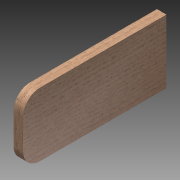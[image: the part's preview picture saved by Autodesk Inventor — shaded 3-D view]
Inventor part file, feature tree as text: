
AUTODESK INVENTOR PART (.ipt)
format: ipt  version: 2014 SP1 (Build 180222100, 222)  size: 101,888 bytes
history: native  units: in
note: dims shown in document units (in); Inventor stores cm internally (conversion verified against a paired STEP export)
features: extrude x1, fillet x1, sketch x1
ambient origin geometry x8: Origin, YZ Plane, XZ Plane, XY Plane, X Axis, Y Axis, Z Axis, Center Point
bodies: Solid1 (feature_tree)
feature tree (3):
  extrude  "Extrusion1"  Depth=0.75in
  fillet  "Fillet1"  Radius=11.25in
  sketch  "Sketch1"  dims[d0=5.0in d1=0.75in d2=11.25in d3=0.0in d4=1.3125in]
